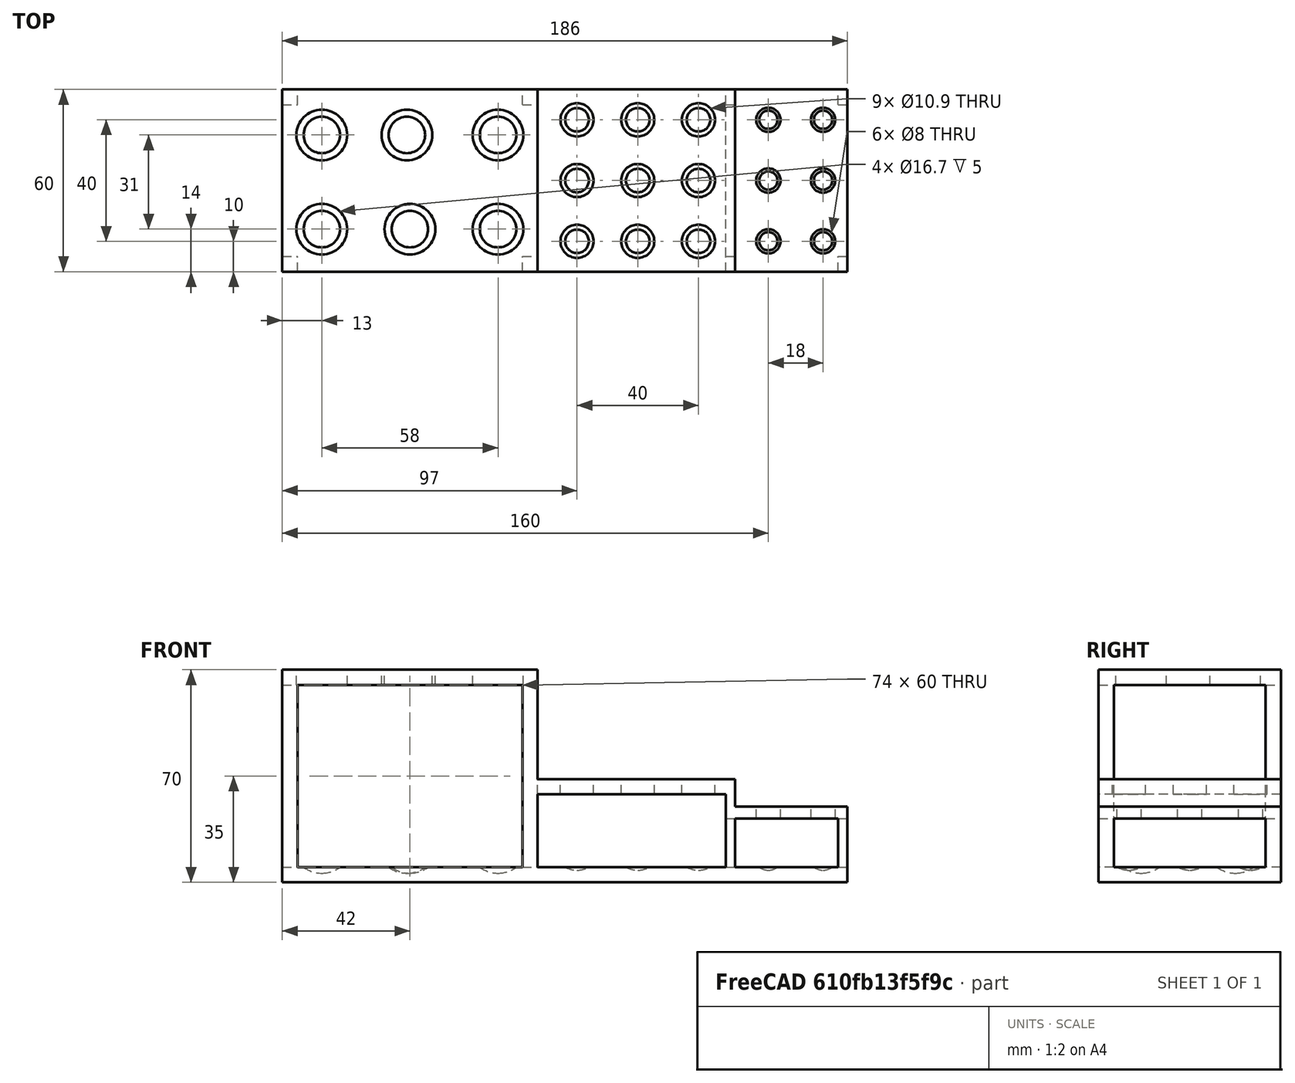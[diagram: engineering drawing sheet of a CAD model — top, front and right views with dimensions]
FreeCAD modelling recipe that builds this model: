
FCSTD DOCUMENT  (FreeCAD 0.18R16093 +53 (Git))
Label: tubes_table
License: All rights reserved
LicenseURL: http://en.wikipedia.org/wiki/All_rights_reserved
objects: Part::Cut×49, Part::Cylinder×21, Part::Sphere×21, Part::Box×9, Part::MultiFuse×1
note: 101 computed .brp shape members not serialized (recipe doc carries the construction recipe); baked Part::Feature solids carry a one-line shape summary decoded from their .brp

FEATURE [Part::Box] Box  label="Cube"
  AttacherType = Attacher::AttachEngine3D
  Height = 70
  Length = 84
  Width = 60
FEATURE [Part::Cylinder] Cylinder
  Angle = 360
  AttacherType = Attacher::AttachEngine3D
  Height = 80
  Placement = pos=(13,14,6) rot=(0,0,1;0rad)
  Radius = 8.35
FEATURE [Part::Cylinder] Cylinder001
  Angle = 360
  AttacherType = Attacher::AttachEngine3D
  Height = 80
  Placement = pos=(42,14,6) rot=(0,0,1;0rad)
  Radius = 8.35
FEATURE [Part::Cylinder] Cylinder002
  Angle = 360
  AttacherType = Attacher::AttachEngine3D
  Height = 80
  Placement = pos=(71,14,7) rot=(0,0,1;0rad)
  Radius = 8.35
FEATURE [Part::Cylinder] Cylinder003
  Angle = 360
  AttacherType = Attacher::AttachEngine3D
  Height = 80
  Placement = pos=(13,45,6) rot=(0,0,1;0rad)
  Radius = 8.35
FEATURE [Part::Cylinder] Cylinder004
  Angle = 360
  AttacherType = Attacher::AttachEngine3D
  Height = 80
  Placement = pos=(41,45,6) rot=(0,0,1;0rad)
  Radius = 8.35
FEATURE [Part::Cylinder] Cylinder005
  Angle = 360
  AttacherType = Attacher::AttachEngine3D
  Height = 80
  Placement = pos=(71,45,6) rot=(0,0,1;0rad)
  Radius = 8.35
FEATURE [Part::Box] Box001  label="Cube001"
  AttacherType = Attacher::AttachEngine3D
  Height = 60
  Length = 74
  Placement = pos=(5,-4,5) rot=(0,0,1;0rad)
  Width = 70
FEATURE [Part::Box] Box002  label="Cube002"
  AttacherType = Attacher::AttachEngine3D
  Height = 60
  Length = 100
  Placement = pos=(-5,5,5) rot=(0,0,1;0rad)
  Width = 50
FEATURE [Part::Cut] Cut
  Base = -> Box
  Tool = -> Cylinder001
FEATURE [Part::Cut] Cut001
  Base = -> Cut
  Tool = -> Cylinder002
FEATURE [Part::Cut] Cut002
  Base = -> Cut001
  Tool = -> Cylinder005
FEATURE [Part::Cut] Cut003
  Base = -> Cut002
  Tool = -> Cylinder004
FEATURE [Part::Cut] Cut004
  Base = -> Cut003
  Tool = -> Cylinder003
FEATURE [Part::Cut] Cut005
  Base = -> Cut004
  Tool = -> Cylinder
FEATURE [Part::Cut] Cut006
  Base = -> Cut005
  Tool = -> Box002
FEATURE [Part::Cut] Cut007
  Base = -> Cut006
  Tool = -> Box001
FEATURE [Part::Box] Box003  label="Cube003"
  AttacherType = Attacher::AttachEngine3D
  Height = 34
  Length = 102
  Placement = pos=(84,0,0) rot=(0,0,1;0rad)
  Width = 60
FEATURE [Part::Cylinder] Cylinder006
  Angle = 360
  AttacherType = Attacher::AttachEngine3D
  Height = 60
  Placement = pos=(97,10,8) rot=(0,0,1;0rad)
  Radius = 5.45
FEATURE [Part::Cylinder] Cylinder007
  Angle = 360
  AttacherType = Attacher::AttachEngine3D
  Height = 60
  Placement = pos=(97,50,8) rot=(0,0,1;0rad)
  Radius = 5.45
FEATURE [Part::Cylinder] Cylinder008
  Angle = 360
  AttacherType = Attacher::AttachEngine3D
  Height = 60
  Placement = pos=(97,30,9) rot=(0,0,1;0rad)
  Radius = 5.45
FEATURE [Part::Cylinder] Cylinder009
  Angle = 360
  AttacherType = Attacher::AttachEngine3D
  Height = 60
  Placement = pos=(117,50,9) rot=(0,0,1;0rad)
  Radius = 5.45
FEATURE [Part::Cylinder] Cylinder010
  Angle = 360
  AttacherType = Attacher::AttachEngine3D
  Height = 60
  Placement = pos=(117,30,9) rot=(0,0,1;0rad)
  Radius = 5.45
FEATURE [Part::Cylinder] Cylinder011
  Angle = 360
  AttacherType = Attacher::AttachEngine3D
  Height = 60
  Placement = pos=(117,10,9) rot=(0,0,1;0rad)
  Radius = 5.45
FEATURE [Part::Cylinder] Cylinder012
  Angle = 360
  AttacherType = Attacher::AttachEngine3D
  Height = 60
  Placement = pos=(137,50,9) rot=(0,0,1;0rad)
  Radius = 5.45
FEATURE [Part::Cylinder] Cylinder013
  Angle = 360
  AttacherType = Attacher::AttachEngine3D
  Height = 60
  Placement = pos=(137,30,9) rot=(0,0,1;0rad)
  Radius = 5.45
FEATURE [Part::Cylinder] Cylinder014
  Angle = 360
  AttacherType = Attacher::AttachEngine3D
  Height = 60
  Placement = pos=(137,10,10) rot=(0,0,1;0rad)
  Radius = 5.45
FEATURE [Part::Box] Box006  label="Cube006"
  AttacherType = Attacher::AttachEngine3D
  Height = 24
  Length = 64
  Placement = pos=(82,-5,5) rot=(0,0,1;0rad)
  Width = 80
FEATURE [Part::Cylinder] Cylinder015
  Angle = 360
  AttacherType = Attacher::AttachEngine3D
  Height = 30
  Placement = pos=(160,10,16) rot=(0,0,1;0rad)
  Radius = 4
FEATURE [Part::Cylinder] Cylinder016
  Angle = 360
  AttacherType = Attacher::AttachEngine3D
  Height = 30
  Placement = pos=(178,10,16) rot=(0,0,1;0rad)
  Radius = 4
FEATURE [Part::Cylinder] Cylinder017
  Angle = 360
  AttacherType = Attacher::AttachEngine3D
  Height = 30
  Placement = pos=(160,30,16) rot=(0,0,1;0rad)
  Radius = 4
FEATURE [Part::Cylinder] Cylinder018
  Angle = 360
  AttacherType = Attacher::AttachEngine3D
  Height = 30
  Placement = pos=(178,30,16) rot=(0,0,1;0rad)
  Radius = 4
FEATURE [Part::Cylinder] Cylinder019
  Angle = 360
  AttacherType = Attacher::AttachEngine3D
  Height = 30
  Placement = pos=(160,50,16) rot=(0,0,1;0rad)
  Radius = 4
FEATURE [Part::Cylinder] Cylinder020
  Angle = 360
  AttacherType = Attacher::AttachEngine3D
  Height = 30
  Placement = pos=(178,50,16) rot=(0,0,1;0rad)
  Radius = 4
FEATURE [Part::Box] Box009  label="Cube009"
  AttacherType = Attacher::AttachEngine3D
  Height = 24
  Length = 75
  Placement = pos=(71,5,5) rot=(0,0,1;0rad)
  Width = 50
FEATURE [Part::Cut] Cut008
  Base = -> Box003
  Tool = -> Box009
FEATURE [Part::Cut] Cut009
  Base = -> Cut008
  Tool = -> Box006
FEATURE [Part::Cut] Cut010
  Base = -> Cut009
  Tool = -> Cylinder012
FEATURE [Part::Cut] Cut011
  Base = -> Cut010
  Tool = -> Cylinder013
FEATURE [Part::Cut] Cut012
  Base = -> Cut011
  Tool = -> Cylinder014
FEATURE [Part::Cut] Cut013
  Base = -> Cut012
  Tool = -> Cylinder009
FEATURE [Part::Cut] Cut014
  Base = -> Cut013
  Tool = -> Cylinder010
FEATURE [Part::Cut] Cut015
  Base = -> Cut014
  Tool = -> Cylinder011
FEATURE [Part::Cut] Cut016
  Base = -> Cut015
  Tool = -> Cylinder007
FEATURE [Part::Cut] Cut017
  Base = -> Cut016
  Tool = -> Cylinder008
FEATURE [Part::Cut] Cut018
  Base = -> Cut017
  Tool = -> Cylinder006
FEATURE [Part::Box] Box008  label="Cube008"
  AttacherType = Attacher::AttachEngine3D
  Height = 16
  Length = 70
  Placement = pos=(183,-3,5) rot=(0,0,1;1.5708rad)
  Width = 34
FEATURE [Part::Box] Box007  label="Cube007"
  AttacherType = Attacher::AttachEngine3D
  Height = 16
  Length = 50
  Placement = pos=(142,5,5) rot=(0,0,1;0rad)
  Width = 50
FEATURE [Part::Cut] Cut019
  Base = -> Cut018
  Tool = -> Box007
FEATURE [Part::Cut] Cut020
  Base = -> Cut019
  Tool = -> Box008
FEATURE [Part::Box] Box010  label="Cube010"
  AttacherType = Attacher::AttachEngine3D
  Height = 10
  Length = 50
  Placement = pos=(149,0,25) rot=(0,0,1;0rad)
  Width = 60
FEATURE [Part::Cut] Cut021
  Base = -> Cut020
  Tool = -> Box010
FEATURE [Part::Cut] Cut022
  Base = -> Cut021
  Tool = -> Cylinder016
FEATURE [Part::Cut] Cut023
  Base = -> Cut022
  Tool = -> Cylinder015
FEATURE [Part::Cut] Cut024
  Base = -> Cut023
  Tool = -> Cylinder017
FEATURE [Part::Cut] Cut025
  Base = -> Cut024
  Tool = -> Cylinder018
FEATURE [Part::Cut] Cut026
  Base = -> Cut025
  Tool = -> Cylinder019
FEATURE [Part::Cut] Cut027
  Base = -> Cut026
  Tool = -> Cylinder020
FEATURE [Part::Sphere] Sphere
  Angle1 = -90
  Angle2 = 90
  Angle3 = 360
  AttacherType = Attacher::AttachEngine3D
  Placement = pos=(13,14,13) rot=(0,0,1;0rad)
  Radius = 10
FEATURE [Part::Sphere] Sphere001
  Angle1 = -90
  Angle2 = 90
  Angle3 = 360
  AttacherType = Attacher::AttachEngine3D
  Placement = pos=(42,14,13) rot=(0,0,1;0rad)
  Radius = 10
FEATURE [Part::Sphere] Sphere002
  Angle1 = -90
  Angle2 = 90
  Angle3 = 360
  AttacherType = Attacher::AttachEngine3D
  Placement = pos=(71,14,13) rot=(0,0,1;0rad)
  Radius = 10
FEATURE [Part::Sphere] Sphere003
  Angle1 = -90
  Angle2 = 90
  Angle3 = 360
  AttacherType = Attacher::AttachEngine3D
  Placement = pos=(13,45,13) rot=(0,0,1;0rad)
  Radius = 10
FEATURE [Part::Sphere] Sphere004
  Angle1 = -90
  Angle2 = 90
  Angle3 = 360
  AttacherType = Attacher::AttachEngine3D
  Placement = pos=(41,45,13) rot=(0,0,1;0rad)
  Radius = 10
FEATURE [Part::Sphere] Sphere005
  Angle1 = -90
  Angle2 = 90
  Angle3 = 360
  AttacherType = Attacher::AttachEngine3D
  Placement = pos=(71,45,13) rot=(0,0,1;0rad)
  Radius = 10
FEATURE [Part::Cut] Cut028
  Base = -> Cut007
  Tool = -> Sphere
FEATURE [Part::Cut] Cut029
  Base = -> Cut028
  Tool = -> Sphere001
FEATURE [Part::Cut] Cut030
  Base = -> Cut029
  Tool = -> Sphere002
FEATURE [Part::Cut] Cut031
  Base = -> Cut030
  Tool = -> Sphere003
FEATURE [Part::Cut] Cut032
  Base = -> Cut031
  Tool = -> Sphere004
FEATURE [Part::Cut] Cut033
  Base = -> Cut032
  Tool = -> Sphere005
FEATURE [Part::Sphere] Sphere006
  Angle1 = -90
  Angle2 = 90
  Angle3 = 360
  AttacherType = Attacher::AttachEngine3D
  Placement = pos=(97,10,12) rot=(0,0,1;0rad)
  Radius = 8
FEATURE [Part::Sphere] Sphere007
  Angle1 = -90
  Angle2 = 90
  Angle3 = 360
  AttacherType = Attacher::AttachEngine3D
  Placement = pos=(117,10,12) rot=(0,0,1;0rad)
  Radius = 8
FEATURE [Part::Sphere] Sphere008
  Angle1 = -90
  Angle2 = 90
  Angle3 = 360
  AttacherType = Attacher::AttachEngine3D
  Placement = pos=(137,10,12) rot=(0,0,1;0rad)
  Radius = 8
FEATURE [Part::Sphere] Sphere009
  Angle1 = -90
  Angle2 = 90
  Angle3 = 360
  AttacherType = Attacher::AttachEngine3D
  Placement = pos=(97,30,12) rot=(0,0,1;0rad)
  Radius = 8
FEATURE [Part::Sphere] Sphere010
  Angle1 = -90
  Angle2 = 90
  Angle3 = 360
  AttacherType = Attacher::AttachEngine3D
  Placement = pos=(117,30,12) rot=(0,0,1;0rad)
  Radius = 8
FEATURE [Part::Sphere] Sphere011
  Angle1 = -90
  Angle2 = 90
  Angle3 = 360
  AttacherType = Attacher::AttachEngine3D
  Placement = pos=(137,30,12) rot=(0,0,1;0rad)
  Radius = 8
FEATURE [Part::Sphere] Sphere012
  Angle1 = -90
  Angle2 = 90
  Angle3 = 360
  AttacherType = Attacher::AttachEngine3D
  Placement = pos=(137,50,12) rot=(0,0,1;0rad)
  Radius = 8
FEATURE [Part::Sphere] Sphere013
  Angle1 = -90
  Angle2 = 90
  Angle3 = 360
  AttacherType = Attacher::AttachEngine3D
  Placement = pos=(117,50,12) rot=(0,0,1;0rad)
  Radius = 8
FEATURE [Part::Sphere] Sphere014
  Angle1 = -90
  Angle2 = 90
  Angle3 = 360
  AttacherType = Attacher::AttachEngine3D
  Placement = pos=(97,50,12) rot=(0,0,1;0rad)
  Radius = 8
FEATURE [Part::Cut] Cut034
  Base = -> Cut027
  Tool = -> Sphere006
FEATURE [Part::Cut] Cut035
  Base = -> Cut034
  Tool = -> Sphere009
FEATURE [Part::Cut] Cut036
  Base = -> Cut035
  Tool = -> Sphere014
FEATURE [Part::Cut] Cut037
  Base = -> Cut036
  Tool = -> Sphere007
FEATURE [Part::Cut] Cut038
  Base = -> Cut037
  Tool = -> Sphere010
FEATURE [Part::Cut] Cut039
  Base = -> Cut038
  Tool = -> Sphere013
FEATURE [Part::Cut] Cut040
  Base = -> Cut039
  Tool = -> Sphere008
FEATURE [Part::Cut] Cut041
  Base = -> Cut040
  Tool = -> Sphere011
FEATURE [Part::Cut] Cut042
  Base = -> Cut041
  Tool = -> Sphere012
FEATURE [Part::Sphere] Sphere015
  Angle1 = -90
  Angle2 = 90
  Angle3 = 360
  AttacherType = Attacher::AttachEngine3D
  Placement = pos=(160,10,9) rot=(0,0,1;0rad)
  Radius = 5
FEATURE [Part::Sphere] Sphere016
  Angle1 = -90
  Angle2 = 90
  Angle3 = 360
  AttacherType = Attacher::AttachEngine3D
  Placement = pos=(160,50,9) rot=(0,0,1;0rad)
  Radius = 5
FEATURE [Part::Sphere] Sphere017
  Angle1 = -90
  Angle2 = 90
  Angle3 = 360
  AttacherType = Attacher::AttachEngine3D
  Placement = pos=(160,30,9) rot=(0,0,1;0rad)
  Radius = 5
FEATURE [Part::Sphere] Sphere018
  Angle1 = -90
  Angle2 = 90
  Angle3 = 360
  AttacherType = Attacher::AttachEngine3D
  Placement = pos=(178,10,9) rot=(0,0,1;0rad)
  Radius = 5
FEATURE [Part::Sphere] Sphere019
  Angle1 = -90
  Angle2 = 90
  Angle3 = 360
  AttacherType = Attacher::AttachEngine3D
  Placement = pos=(178,50,9) rot=(0,0,1;0rad)
  Radius = 5
FEATURE [Part::Sphere] Sphere020
  Angle1 = -90
  Angle2 = 90
  Angle3 = 360
  AttacherType = Attacher::AttachEngine3D
  Placement = pos=(178,30,9) rot=(0,0,1;0rad)
  Radius = 5
FEATURE [Part::Cut] Cut043
  Base = -> Cut042
  Tool = -> Sphere015
FEATURE [Part::Cut] Cut044
  Base = -> Cut043
  Tool = -> Sphere017
FEATURE [Part::Cut] Cut045
  Base = -> Cut044
  Tool = -> Sphere016
FEATURE [Part::Cut] Cut046
  Base = -> Cut045
  Tool = -> Sphere019
FEATURE [Part::Cut] Cut047
  Base = -> Cut046
  Tool = -> Sphere020
FEATURE [Part::Cut] Cut048
  Base = -> Cut047
  Tool = -> Sphere018
FEATURE [Part::MultiFuse] Fusion
  Shapes = -> [Cut033,Cut048]
